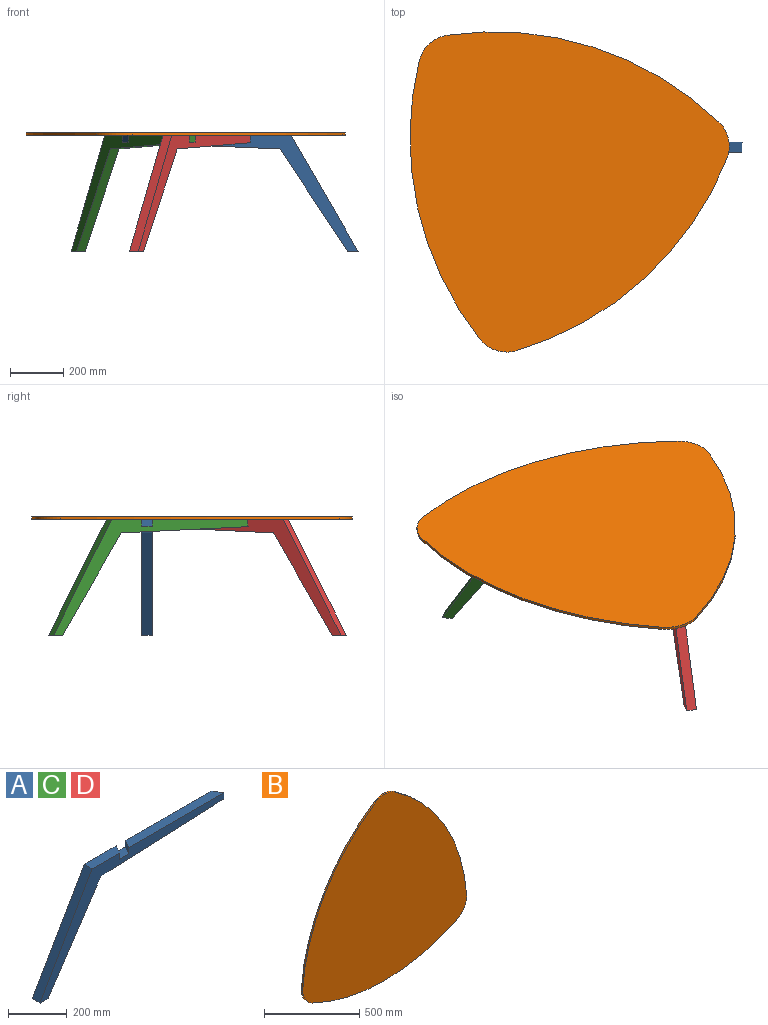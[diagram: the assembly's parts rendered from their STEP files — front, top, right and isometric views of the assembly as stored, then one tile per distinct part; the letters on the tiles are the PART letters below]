
ASSEMBLY  parts=4 mates=7
PART A: 14 faces, bbox 886.1x38.1x435 mm
  f0: plane 38.1x25.4mm, normal (0.87,0.5,0), area 1117.4mm2, adj f1,f4,f5,f13
  f1: plane 864.14x434.98mm, normal (0,1,0), area 44806.5mm2, adj f0,f2,f3,f4,f6,f7,f8,f9
  f2: plane 547.85x38.1mm, normal (0.04,0,-1), area 20472.9mm2, adj f1,f5,f8,f12
  f3: plane 153.58x38.1mm, normal (0,0,1), area 5432.3mm2, adj f1,f5,f6,f9
  f4: plane 459.43x38.1mm, normal (0,0,1), area 16666mm2, adj f0,f1,f5,f10
  f5: plane 886.13x434.98mm, normal (0,-1,0), area 45417.8mm2, adj f0,f2,f3,f4,f6,f7,f8,f9
  f6: plane 434.98x251.13mm, normal (-0.87,0,0.5), area 19136.3mm2, adj f1,f3,f5,f7
  f7: plane 38.1x38.1mm, normal (0,0,-1), area 1451.6mm2, adj f1,f5,f6,f8
  f8: plane 384.18x255.45mm, normal (0.83,0,-0.55), area 17577.6mm2, adj f1,f2,f5,f7
  f9: plane 38.1x25.4mm, normal (0.87,-0.5,0), area 1117.4mm2, adj f1,f3,f5,f11
  f10: plane 38.1x25.4mm, normal (-0.87,0.5,0), area 1117.4mm2, adj f1,f4,f5,f11
  f11: plane 65.99x38.1mm, normal (0,0,1), area 1676.1mm2, adj f1,f5,f9,f10
  f12: plane 38.1x22mm, normal (0.87,0.5,0), area 105.1mm2, adj f1,f2,f5,f13
  f13: plane 66.72x38.1mm, normal (0,0,-1), area 1704.1mm2, adj f0,f1,f5,f12
PART B: 8 faces, bbox 1214.1x9.5x1196.6 mm
  f0: cylinder r=1219.2mm len=1071.71mm, axis (0,1,0), area 10569mm2, adj f3,f4,f5,f7
  f1: cylinder r=1219.2mm len=928.13mm, axis (0,1,0), area 10569mm2, adj f3,f4,f5,f6
  f2: cylinder r=1219.2mm len=928.13mm, axis (0,1,0), area 10569mm2, adj f3,f4,f6,f7
  f3: plane 1214.07x1196.59mm, normal (0,-1,0), area 1044204.1mm2, adj f0,f1,f2,f5,f6,f7
  f4: plane 1214.07x1196.59mm, normal (0,1,0), area 1044204.1mm2, adj f0,f1,f2,f5,f6,f7
  f5: cylinder r=127mm len=122.77mm, axis (0,1,0), area 1432.6mm2, adj f0,f1,f3,f4
  f6: cylinder r=127mm len=141.77mm, axis (0,1,0), area 1432.6mm2, adj f1,f2,f3,f4
  f7: cylinder r=127mm len=122.77mm, axis (0,1,0), area 1432.6mm2, adj f0,f2,f3,f4
PART C: same geometry as A
PART D: same geometry as A
PLACE A rot(axis=(0,0,1),180deg) t=(444.07,-18.63,-250.37)mm
PLACE B rot(axis=(0.98,-0.15,-0.15),91.4deg) t=(-165.36,220.06,194.13)mm
PLACE C rot(axis=(0,0,-1),60deg) t=(-600.42,369.96,-250.37)mm
PLACE D rot(axis=(0,0,1),60deg) t=(-414.7,-728.89,-250.37)mm
MATE planar A.f3 <-> D.f4  axis (0,0,1) through (121.51,-0.07,184.61)mm
MATE planar C.f5 <-> A.f0  axis (-0.87,-0.5,0) through (-474.96,76.45,184.61)mm
MATE planar A.f5 <-> D.f0  axis (0,1,0) through (91.17,19.47,69.63)mm
MATE planar B.f3 <-> D.f4  axis (0,0,-1) through (-272.31,-115.25,184.61)mm
MATE planar C.f3 <-> A.f3  axis (0,0,1) through (-455.21,81.33,184.61)mm
MATE planar D.f5 <-> C.f0  axis (0.87,-0.5,0) through (-223.25,-473.48,184.61)mm
MATE planar A.f1 <-> C.f10  axis (0,-1,0) through (-212.35,-18.63,184.61)mm
